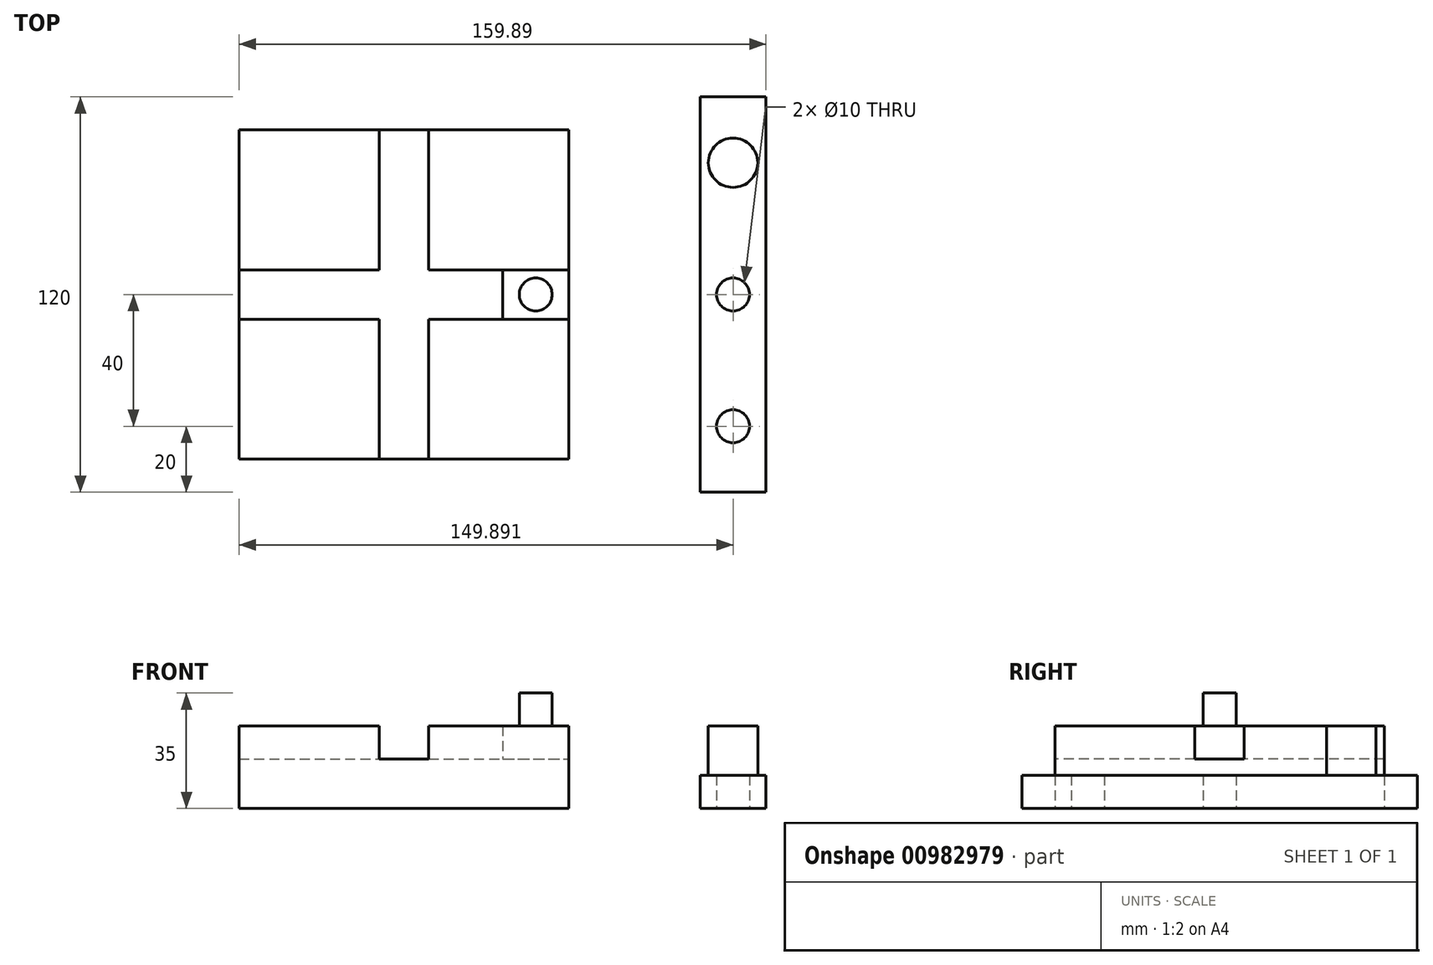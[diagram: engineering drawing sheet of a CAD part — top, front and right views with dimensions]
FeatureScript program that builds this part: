
annotation { "Feature Type Name" : "Feature", "Feature Type Description" : "" }
export const myFeature = defineFeature(function(context is Context, id is Id, definition is map)
    precondition{}
    {
        {
            var Q0;
            Q0=qCreatedBy(makeId("Top.planeOp"),FACE);
            var sketch = newSketch(context, id + "F0", { "sketchPlane" : qUnion([Q0])});
            skLineSegment(sketch, "E0.bottom", {"start": v(50, -50) * mm, "end": v(-50, -50) * mm});
            skLineSegment(sketch, "E0.top", {"start": v(50, 50) * mm, "end": v(-50, 50) * mm});
            skLineSegment(sketch, "E0.left", {"start": v(50, -50) * mm, "end": v(50, 50) * mm});
            skLineSegment(sketch, "E0.right", {"start": v(-50, -50) * mm, "end": v(-50, 50) * mm});
            skPoint(sketch, "E0.middle", {"position": v(0, 0) * mm});
            skSolve(sketch);
        }
        {
            var Q0;
            Q0=makeQuery(id+"F0.imprint","IMPRINT",FACE,{"disambiguationData":[TD([[makeQuery(id+"F0.imprint","IMPRINT",EDGE,{"derivedFrom":sQuery(id+"F0.wireOp",EDGE,"E0.bottom")}),-1.0]])]});
            extrude(context, id + "F1", {"entities" : qUnion([Q0]), "depth" : 25 * mm, "offsetDistance" : 25 * mm});
        }
        {
            var Q0;
            Q0=makeQuery(id+"F1.opExtrude","SWEPT_FACE",FACE,{"disambiguationData":[OSD([sQuery(id+"F0.wireOp",EDGE,"E0.left")])]});
            var sketch = newSketch(context, id + "F2", { "sketchPlane" : qUnion([Q0])});
            skLineSegment(sketch, "E1.bottom", {"start": v(7.5, 25) * mm, "end": v(-7.5, 25) * mm});
            skLineSegment(sketch, "E1.top", {"start": v(7.5, 15) * mm, "end": v(-7.5, 15) * mm});
            skLineSegment(sketch, "E1.left", {"start": v(7.5, 25) * mm, "end": v(7.5, 15) * mm});
            skLineSegment(sketch, "E1.right", {"start": v(-7.5, 25) * mm, "end": v(-7.5, 15) * mm});
            skPoint(sketch, "E1.middle", {"position": v(0, 20) * mm});
            skPoint(sketch, "E1.middle.positionSnap0", {"position": v(0, 25) * mm});
            skPoint(sketch, "E1.centerSnap0", {"position": v(0, 25) * mm});
            skSolve(sketch);
        }
        {
            var Q0;
            Q0=makeQuery(id+"F2.imprint","IMPRINT",FACE,{"disambiguationData":[TD([[makeQuery(id+"F2.imprint","IMPRINT",EDGE,{"derivedFrom":sQuery(id+"F2.wireOp",EDGE,"E1.bottom")}),-1.0]])]});
            extrude(context, id + "F3", {"entities" : qUnion([Q0]), "operationType" : NewBodyOperationType.REMOVE, "endBound" : BoundingType.UP_TO_NEXT, "oppositeDirection" : true, "depth" : 25 * mm, "offsetDistance" : 25 * mm});
        }
        {
            var Q0;
            Q0=makeQuery(id+"F1.opExtrude","SWEPT_FACE",FACE,{"disambiguationData":[OSD([sQuery(id+"F0.wireOp",EDGE,"E0.bottom")])]});
            var sketch = newSketch(context, id + "F4", { "sketchPlane" : qUnion([Q0])});
            skLineSegment(sketch, "E2.bottom", {"start": v(7.5, 25) * mm, "end": v(-7.5, 25) * mm});
            skLineSegment(sketch, "E2.top", {"start": v(7.5, 15) * mm, "end": v(-7.5, 15) * mm});
            skLineSegment(sketch, "E2.left", {"start": v(7.5, 25) * mm, "end": v(7.5, 15) * mm});
            skLineSegment(sketch, "E2.right", {"start": v(-7.5, 25) * mm, "end": v(-7.5, 15) * mm});
            skPoint(sketch, "E2.middle", {"position": v(0, 20) * mm});
            skPoint(sketch, "E2.middle.positionSnap0", {"position": v(0, 25) * mm});
            skPoint(sketch, "E2.centerSnap0", {"position": v(0, 25) * mm});
            skSolve(sketch);
        }
        {
            var Q0;
            Q0=makeQuery(id+"F4.imprint","IMPRINT",FACE,{"disambiguationData":[TD([[makeQuery(id+"F4.imprint","IMPRINT",EDGE,{"derivedFrom":sQuery(id+"F4.wireOp",EDGE,"E2.bottom")}),1.0]])]});
            var Q1;
            Q1=makeQuery(id+"F1.opExtrude","SWEPT_FACE",FACE,{"disambiguationData":[OSD([sQuery(id+"F0.wireOp",EDGE,"E0.top")])]});
            extrude(context, id + "F5", {"entities" : qUnion([Q0]), "operationType" : NewBodyOperationType.REMOVE, "endBound" : BoundingType.UP_TO_SURFACE, "oppositeDirection" : true, "depth" : 25 * mm, "endBoundEntityFace" : qUnion([Q1]), "offsetDistance" : 25 * mm});
        }
        {
            var Q0;
            Q0=makeQuery(id+"F2.imprint","IMPRINT",FACE,{"disambiguationData":[TD([[makeQuery(id+"F2.imprint","IMPRINT",EDGE,{"derivedFrom":sQuery(id+"F2.wireOp",EDGE,"E1.bottom")}),-1.0]])]});
            extrude(context, id + "F6", {"entities" : qUnion([Q0]), "oppositeDirection" : true, "depth" : 20 * mm, "offsetDistance" : 25 * mm});
        }
        {
            var Q0;
            Q0=makeQuery(id+"F6.opExtrude","SWEPT_FACE",FACE,{"disambiguationData":[OSD([sQuery(id+"F2.wireOp",EDGE,"E1.bottom")])]});
            var sketch = newSketch(context, id + "F7", { "sketchPlane" : qUnion([Q0])});
            skCircle(sketch, "E3", {"center": v(40, 0) * mm, "radius": 5 * mm});
            skPoint(sketch, "E3.centerSnap0", {"position": v(40, -7.5) * mm});
            skPoint(sketch, "E3.centerSnap1", {"position": v(30, 0) * mm});
            skSolve(sketch);
        }
        {
            var Q0;
            Q0=makeQuery(id+"F7.imprint","IMPRINT",FACE,{"disambiguationData":[TD([[makeQuery(id+"F7.imprint","IMPRINT",EDGE,{"derivedFrom":sQuery(id+"F7.wireOp",EDGE,"E3")}),1.0]])]});
            extrude(context, id + "F8", {"entities" : qUnion([Q0]), "operationType" : NewBodyOperationType.ADD, "depth" : 10 * mm, "offsetDistance" : 25 * mm});
        }
        {
            var Q0;
            Q0=qCreatedBy(makeId("Top.planeOp"),FACE);
            var sketch = newSketch(context, id + "F9", { "sketchPlane" : qUnion([Q0])});
            skLineSegment(sketch, "E4.bottom", {"start": v(109.9, -60) * mm, "end": v(89.9, -60) * mm});
            skLineSegment(sketch, "E4.top", {"start": v(109.9, 60) * mm, "end": v(89.9, 60) * mm});
            skLineSegment(sketch, "E4.left", {"start": v(109.9, -60) * mm, "end": v(109.9, 60) * mm});
            skLineSegment(sketch, "E4.right", {"start": v(89.9, -60) * mm, "end": v(89.9, 60) * mm});
            skPoint(sketch, "E4.middle", {"position": v(99.9, 0) * mm});
            skCircle(sketch, "E5", {"center": v(99.9, 0) * mm, "radius": 5 * mm});
            skCircle(sketch, "E6", {"center": v(99.9, -40) * mm, "radius": 5 * mm});
            skSolve(sketch);
        }
        {
            var Q0;
            Q0=makeQuery(id+"F9.imprint","IMPRINT",FACE,{"disambiguationData":[TD([[makeQuery(id+"F9.imprint","IMPRINT",EDGE,{"derivedFrom":sQuery(id+"F9.wireOp",EDGE,"E4.bottom")}),-1.0]])]});
            extrude(context, id + "F10", {"entities" : qUnion([Q0]), "depth" : 10 * mm, "offsetDistance" : 25 * mm});
        }
        {
            var Q0;
            Q0=makeQuery(id+"F10.opExtrude","CAP_FACE",FACE,{"disambiguationData":[OSD([sQuery(id+"F9.wireOp",EDGE,"E4.bottom"),sQuery(id+"F9.wireOp",EDGE,"E4.top"),sQuery(id+"F9.wireOp",EDGE,"E4.left"),sQuery(id+"F9.wireOp",EDGE,"E4.right"),sQuery(id+"F9.wireOp",EDGE,"E5"),sQuery(id+"F9.wireOp",EDGE,"E6")])],"isStart":false});
            var sketch = newSketch(context, id + "F11", { "sketchPlane" : qUnion([Q0])});
            skCircle(sketch, "E7", {"center": v(99.9, 40) * mm, "radius": 7.5 * mm});
            skPoint(sketch, "E7.centerSnap0", {"position": v(99.9, 60) * mm});
            skSolve(sketch);
        }
        {
            var Q0;
            Q0=makeQuery(id+"F11.imprint","IMPRINT",FACE,{"disambiguationData":[TD([[makeQuery(id+"F11.imprint","IMPRINT",EDGE,{"derivedFrom":sQuery(id+"F11.wireOp",EDGE,"E7")}),1.0]])]});
            extrude(context, id + "F12", {"entities" : qUnion([Q0]), "operationType" : NewBodyOperationType.ADD, "depth" : 15 * mm, "offsetDistance" : 25 * mm});
        }
    });
